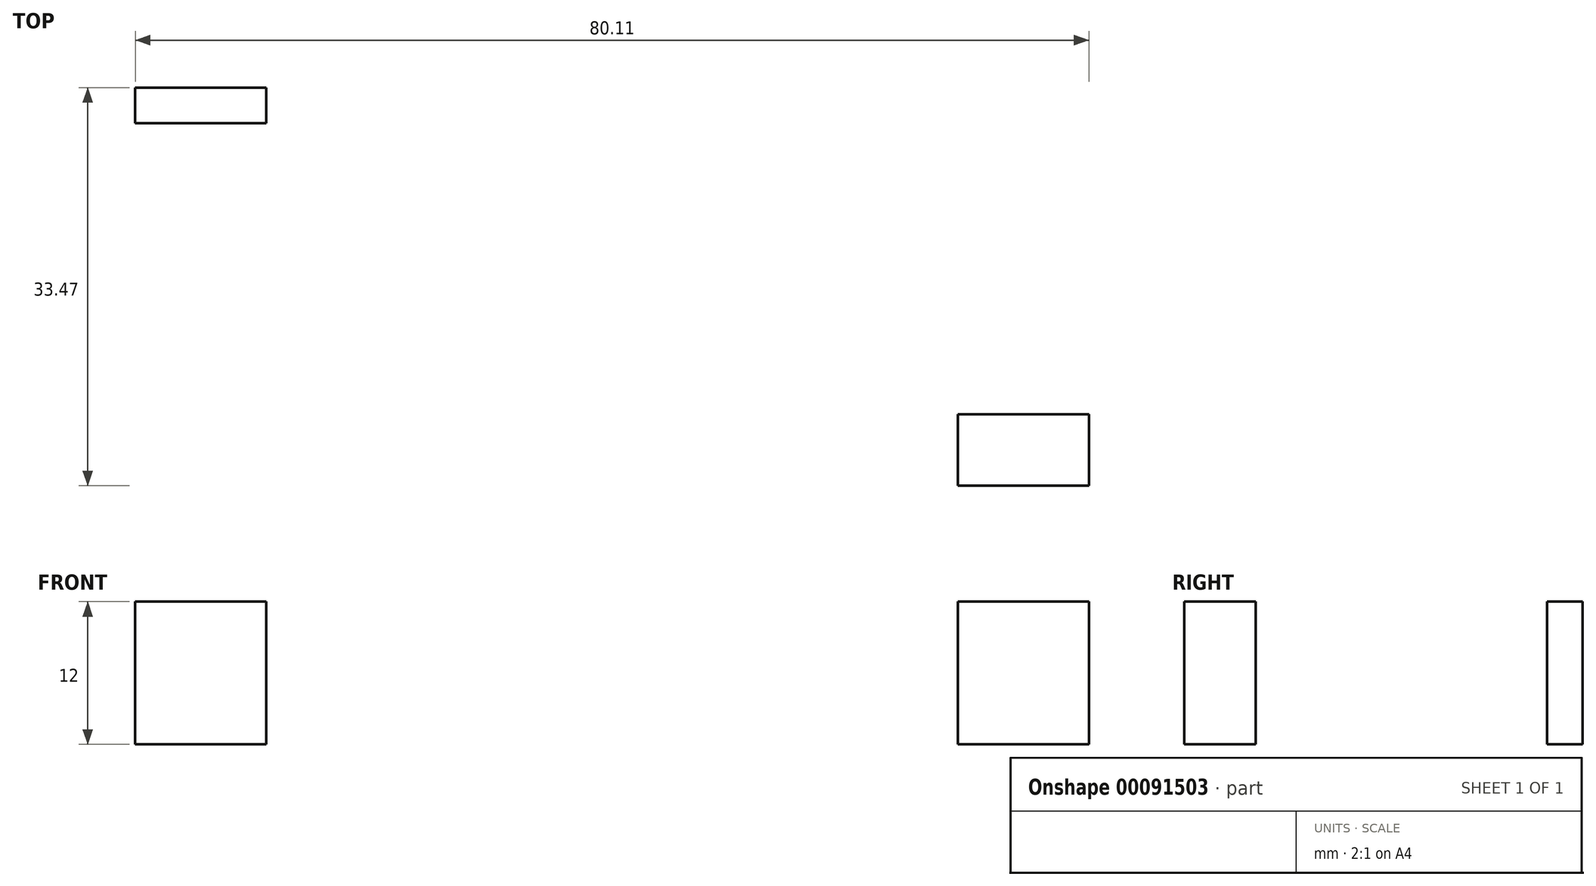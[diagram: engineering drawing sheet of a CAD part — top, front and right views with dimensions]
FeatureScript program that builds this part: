
annotation { "Feature Type Name" : "Feature", "Feature Type Description" : "" }
export const myFeature = defineFeature(function(context is Context, id is Id, definition is map)
    precondition{}
    {
        {
            var Q0;
            Q0=qCreatedBy(makeId("Top.planeOp"),FACE);
            var sketch = newSketch(context, id + "F0", { "sketchPlane" : qUnion([Q0])});
            skLineSegment(sketch, "E0", {"start": v(-48.46, 25.02) * mm, "end": v(-48.46, 28.02) * mm});
            skLineSegment(sketch, "E1", {"start": v(-48.46, 28.02) * mm, "end": v(-37.46, 28.02) * mm});
            skLineSegment(sketch, "E2", {"start": v(-48.46, 25.02) * mm, "end": v(-37.46, 25.02) * mm});
            skLineSegment(sketch, "E3", {"start": v(-37.46, 28.02) * mm, "end": v(-37.46, 25.02) * mm});
            skLineSegment(sketch, "E4", {"start": v(20.65, -5.45) * mm, "end": v(20.65, 0.55) * mm});
            skLineSegment(sketch, "E5", {"start": v(20.65, 0.55) * mm, "end": v(31.65, 0.55) * mm});
            skLineSegment(sketch, "E6", {"start": v(20.65, -5.45) * mm, "end": v(31.65, -5.45) * mm});
            skLineSegment(sketch, "E7", {"start": v(31.65, 0.55) * mm, "end": v(31.65, -5.45) * mm});
            skSolve(sketch);
        }
        {
            var Q0;
            Q0=makeQuery(id+"F0.imprint","IMPRINT",FACE,{"disambiguationData":[TD([[makeQuery(id+"F0.imprint","IMPRINT",EDGE,{"derivedFrom":sQuery(id+"F0.wireOp",EDGE,"E0")}),-1.0]])]});
            var Q1;
            Q1=makeQuery(id+"F0.imprint","IMPRINT",FACE,{"disambiguationData":[TD([[makeQuery(id+"F0.imprint","IMPRINT",EDGE,{"derivedFrom":sQuery(id+"F0.wireOp",EDGE,"E4")}),-1.0]])]});
            extrude(context, id + "F1", {"entities" : qUnion([Q0, Q1]), "depth" : 12 * mm});
        }
    });
